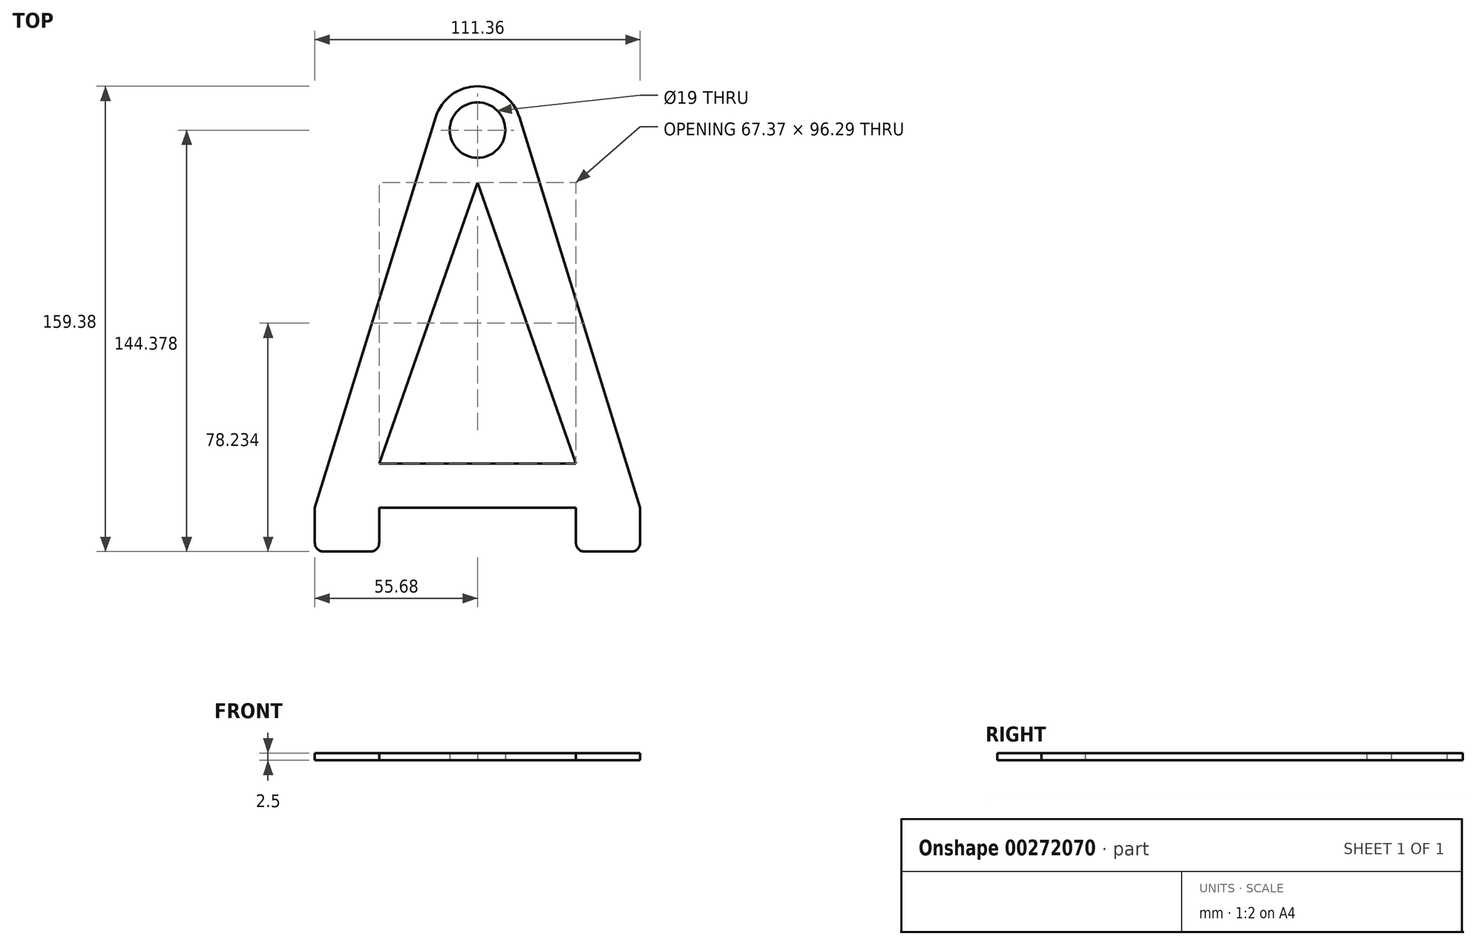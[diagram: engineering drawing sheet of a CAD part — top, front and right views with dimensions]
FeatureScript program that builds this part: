
annotation { "Feature Type Name" : "Feature", "Feature Type Description" : "" }
export const myFeature = defineFeature(function(context is Context, id is Id, definition is map)
    precondition{}
    {
        {
            var Q0;
            Q0=qCreatedBy(makeId("Top.planeOp"),FACE);
            var sketch = newSketch(context, id + "F0", { "sketchPlane" : qUnion([Q0])});
            skCircle(sketch, "E0", {"center": v(0, 64.36) * mm, "radius": 9.5 * mm});
            skCircle(sketch, "E1", {"center": v(0, 64.36) * mm, "radius": 15 * mm});
            skLineSegment(sketch, "E2", {"start": v(-14.33, 68.79) * mm, "end": v(-55.68, -64.93) * mm});
            skLineSegment(sketch, "E3", {"start": v(-55.68, -64.93) * mm, "end": v(-55.68, -77.02) * mm});
            skLineSegment(sketch, "E4", {"start": v(-33.68, -77.02) * mm, "end": v(-33.68, -64.93) * mm});
            skLineSegment(sketch, "E5.MirrorCS", {"start": v(14.33, 68.79) * mm, "end": v(55.68, -64.93) * mm});
            skLineSegment(sketch, "E6.MirrorCS", {"start": v(55.68, -64.93) * mm, "end": v(55.68, -77.02) * mm});
            skLineSegment(sketch, "E7.MirrorCS", {"start": v(33.68, -77.02) * mm, "end": v(33.68, -64.93) * mm});
            skLineSegment(sketch, "E8", {"start": v(-33.68, -64.93) * mm, "end": v(33.68, -64.93) * mm});
            skLineSegment(sketch, "E9", {"start": v(-52.68, -80.02) * mm, "end": v(-36.68, -80.02) * mm});
            skLineSegment(sketch, "E10", {"start": v(36.68, -80.02) * mm, "end": v(52.68, -80.02) * mm});
            skPoint(sketch, "E11.visualSharp", {"position": v(-55.68, -80.02) * mm});
            skArc(sketch, "E11.filletArc", {"start": v(-55.68, -77.02) * mm, "mid": v(-54.8, -79.14) * mm, "end": v(-52.68, -80.02) * mm});
            skPoint(sketch, "E12.visualSharp", {"position": v(-33.68, -80.02) * mm});
            skArc(sketch, "E12.filletArc", {"start": v(-36.68, -80.02) * mm, "mid": v(-34.56, -79.14) * mm, "end": v(-33.68, -77.02) * mm});
            skPoint(sketch, "E13.visualSharp", {"position": v(33.68, -80.02) * mm});
            skArc(sketch, "E13.filletArc", {"start": v(33.68, -77.02) * mm, "mid": v(34.56, -79.14) * mm, "end": v(36.68, -80.02) * mm});
            skPoint(sketch, "E14.visualSharp", {"position": v(55.68, -80.02) * mm});
            skArc(sketch, "E14.filletArc", {"start": v(52.68, -80.02) * mm, "mid": v(54.8, -79.14) * mm, "end": v(55.68, -77.02) * mm});
            skPoint(sketch, "E15", {"position": v(0, -64.93) * mm});
            skLineSegment(sketch, "E16", {"start": v(0, -49.93) * mm, "end": v(-33.68, -49.93) * mm});
            skLineSegment(sketch, "E17", {"start": v(-33.68, -49.93) * mm, "end": v(0, 46.36) * mm});
            skLineSegment(sketch, "E18.MirrorCS", {"start": v(33.68, -49.93) * mm, "end": v(0, 46.36) * mm});
            skLineSegment(sketch, "E19.MirrorCS", {"start": v(0, -49.93) * mm, "end": v(33.68, -49.93) * mm});
            skSolve(sketch);
        }
        {
            var Q0;
            Q0=makeQuery(id+"F0.imprint","IMPRINT",FACE,{"disambiguationData":[TD([[makeQuery(id+"F0.imprint","IMPRINT",EDGE,{"derivedFrom":sQuery(id+"F0.wireOp",EDGE,"E0")}),-1.0]])]});
            var Q1;
            {var subQ1=sQuery(id+"F0.wireOp",EDGE,"E2");Q1=makeQuery(id+"F0.imprint","IMPRINT",FACE,{"disambiguationData":[TD([[makeQuery(id+"F0.imprint","IMPRINT",EDGE,{"derivedFrom":subQ1}),1.0]])]});}
            extrude(context, id + "F1", {"entities" : qUnion([Q0, Q1]), "depth" : 2.5 * mm});
        }
    });
